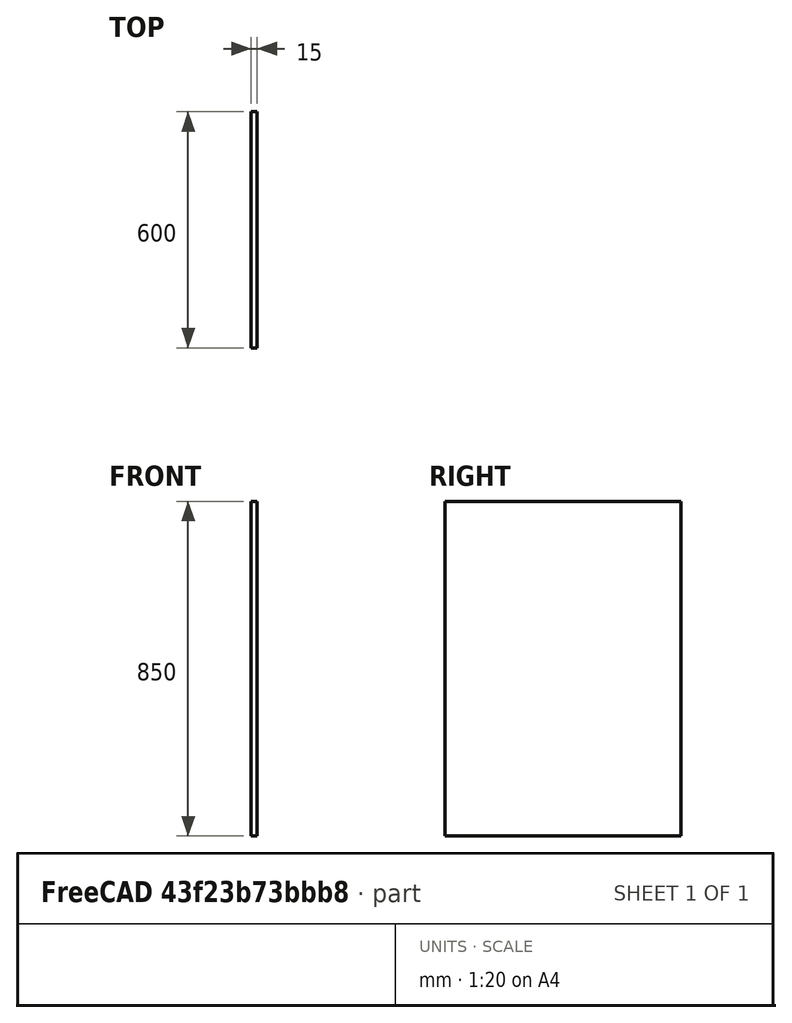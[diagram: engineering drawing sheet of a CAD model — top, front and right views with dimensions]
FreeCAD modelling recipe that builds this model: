
FCSTD DOCUMENT  (FreeCAD 1.0R39319 (Git))
Label: front
License: All rights reserved
LicenseURL: http://en.wikipedia.org/wiki/All_rights_reserved
objects: Sketcher::SketchObject×1, PartDesign::Pad×1, PartDesign::Body×1
note: 6 computed .brp shape members not serialized (recipe doc carries the construction recipe); baked Part::Feature solids carry a one-line shape summary decoded from their .brp

FEATURE [Sketcher::SketchObject] Sketch  label="front_sketch"
  ArcFitTolerance = 0
  AttachmentSupport = -> [YZ_Plane]
  FullyConstrained = true
  MakeInternals = false
  MapMode = 5
  Placement = pos=(0,0,0) rot=(0.57735,0.57735,0.57735;2.0944rad)
  sketch-geometry (4):
    g0: LineSegment StartX=0 StartY=0 StartZ=0 EndX=600 EndY=0 EndZ=0
    g1: LineSegment StartX=600 StartY=0 StartZ=0 EndX=600 EndY=850 EndZ=0
    g2: LineSegment StartX=600 StartY=850 StartZ=0 EndX=0 EndY=850 EndZ=0
    g3: LineSegment StartX=0 StartY=850 StartZ=0 EndX=0 EndY=0 EndZ=0
  constraints (11):
    c: Coincident(g0,g1)
    c: Coincident(g1,g2)
    c: Coincident(g2,g3)
    c: Coincident(g3,g0)
    c: Horizontal(g0)
    c: Horizontal(g2)
    c: Vertical(g1)
    c: Vertical(g3)
    c: Coincident(g0,g-1)
    c: DistanceX(g0,g0) = 600
    c: DistanceY(g3,g3) = 850
FEATURE [PartDesign::Pad] Pad  label="front_pad"
  AllowMultiFace = false
  Direction = (1,-1.129e-13,1.129e-13)
  Length = 15
  Length2 = 100
  Placement = pos=(0,0,0) rot=(0.57735,0.57735,0.57735;2.0944rad)
  Profile = -> Sketch
  Suppressed = false
  Type = 0
FEATURE [PartDesign::Body] Body  label="front_body"
  AllowCompound = false
  Group = -> [Sketch,Pad]
  Origin = -> Origin
  Tip = -> Pad
